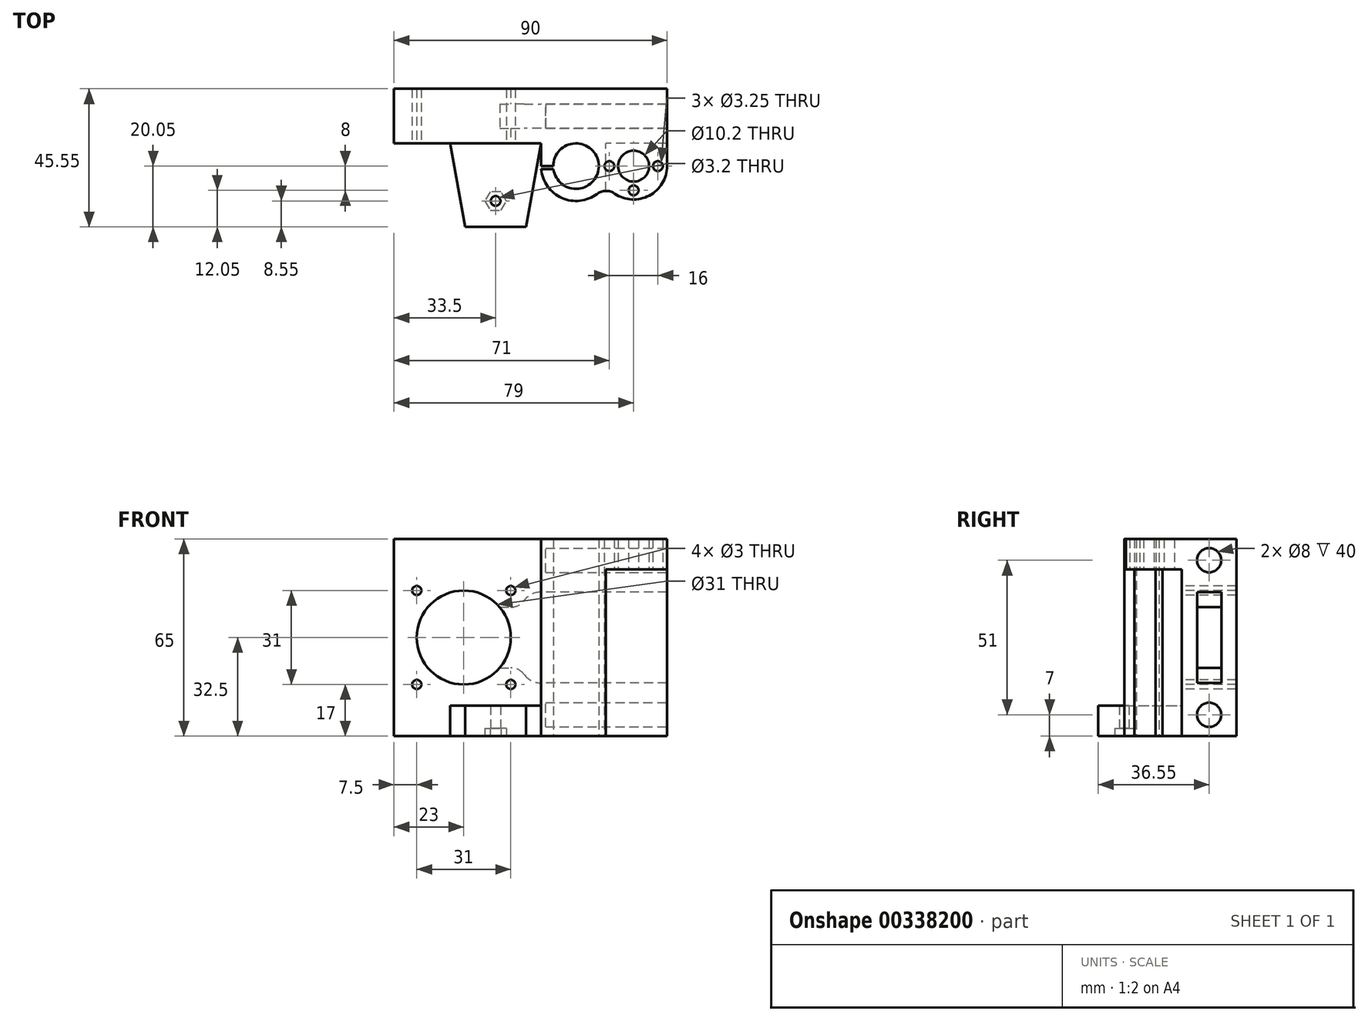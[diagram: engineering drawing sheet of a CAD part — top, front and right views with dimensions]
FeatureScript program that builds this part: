
annotation { "Feature Type Name" : "Feature", "Feature Type Description" : "" }
export const myFeature = defineFeature(function(context is Context, id is Id, definition is map)
    precondition{}
    {
        {
            var Q0;
            Q0=qCreatedBy(makeId("Top.planeOp"),FACE);
            var sketch = newSketch(context, id + "F0", { "sketchPlane" : qUnion([Q0])});
            skLineSegment(sketch, "E0.top", {"start": v(0, 18) * mm, "end": v(-90, 18) * mm});
            skLineSegment(sketch, "E0.left", {"start": v(0, 0) * mm, "end": v(0, 18) * mm});
            skLineSegment(sketch, "E0.right", {"start": v(-90, 0) * mm, "end": v(-90, 18) * mm});
            skArc(sketch, "E1", {"start": v(-17.24, -16.56) * mm, "mid": v(-5.88, -17.24) * mm, "end": v(0, -7.5) * mm});
            skLineSegment(sketch, "E2.left", {"start": v(-41.5, -7.5) * mm, "end": v(-41.5, 0) * mm});
            skLineSegment(sketch, "E2.right", {"start": v(0, -7.5) * mm, "end": v(0, 0) * mm});
            skLineSegment(sketch, "E3", {"start": v(-30, -7.5) * mm, "end": v(-11, -7.5) * mm, "construction": true});
            skCircle(sketch, "E4", {"center": v(-11, -7.5) * mm, "radius": 5.1 * mm});
            skCircle(sketch, "E5", {"center": v(-19, -7.5) * mm, "radius": 1.63 * mm});
            skCircle(sketch, "E6.1.0", {"center": v(-11, -15.5) * mm, "radius": 1.63 * mm});
            skCircle(sketch, "E6.2.0", {"center": v(-3, -7.5) * mm, "radius": 1.63 * mm});
            skArc(sketch, "E7", {"start": v(-37.43, -8.5) * mm, "mid": v(-22.52, -7) * mm, "end": v(-37.5, -7.5) * mm});
            skArc(sketch, "E8.trimOffspring", {"start": v(-41.46, -8.5) * mm, "mid": v(-34.68, -18) * mm, "end": v(-23.08, -16.69) * mm});
            skPoint(sketch, "E9.visualSharp", {"position": v(-20.2, -13.52) * mm});
            skArc(sketch, "E9.filletArc", {"start": v(-17.24, -16.56) * mm, "mid": v(-20.18, -15.68) * mm, "end": v(-23.08, -16.69) * mm});
            skLineSegment(sketch, "E10.trimOffspring", {"start": v(-41.5, 0) * mm, "end": v(-90, 0) * mm});
            skLineSegment(sketch, "E11.bottom", {"start": v(-37.5, -7.5) * mm, "end": v(-41.5, -7.5) * mm});
            skLineSegment(sketch, "E11.top", {"start": v(-37.43, -8.5) * mm, "end": v(-41.46, -8.5) * mm});
            skSolve(sketch);
        }
        {
            var Q0;
            Q0=makeQuery(id+"F0.imprint","IMPRINT",FACE,{"disambiguationData":[TD([[makeQuery(id+"F0.imprint","IMPRINT",EDGE,{"derivedFrom":sQuery(id+"F0.wireOp",EDGE,"E0.top")}),1.0]])]});
            extrude(context, id + "F1", {"entities" : qUnion([Q0]), "depth" : 65 * mm});
        }
        {
            var Q0;
            Q0=makeQuery(id+"F1.opExtrude","SWEPT_FACE",FACE,{"disambiguationData":[OSD([sQuery(id+"F0.wireOp",EDGE,"E10.trimOffspring")])]});
            var sketch = newSketch(context, id + "F2", { "sketchPlane" : qUnion([Q0])});
            skLineSegment(sketch, "E12.bottom", {"start": v(0, 0) * mm, "end": v(-20.18, 0) * mm});
            skLineSegment(sketch, "E12.top", {"start": v(0, 55) * mm, "end": v(-20.18, 55) * mm});
            skLineSegment(sketch, "E12.left", {"start": v(0, 0) * mm, "end": v(0, 55) * mm});
            skLineSegment(sketch, "E12.right", {"start": v(-20.18, 0) * mm, "end": v(-20.18, 55) * mm});
            skSolve(sketch);
        }
        {
            var Q0;
            Q0 = qSketchRegion(id + "F2", true);
            extrude(context, id + "F3", {"entities" : qUnion([Q0]), "operationType" : NewBodyOperationType.REMOVE, "endBound" : BoundingType.THROUGH_ALL, "depth" : 25 * mm});
        }
        {
            var Q0;
            Q0=makeQuery(id+"F1.opExtrude","SWEPT_FACE",FACE,{"disambiguationData":[OSD([sQuery(id+"F0.wireOp",EDGE,"E10.trimOffspring")])]});
            var sketch = newSketch(context, id + "F4", { "sketchPlane" : qUnion([Q0])});
            skCircle(sketch, "E13", {"center": v(-67, 32.5) * mm, "radius": 15.5 * mm});
            skCircle(sketch, "E14", {"center": v(-82.5, 17) * mm, "radius": 1.5 * mm});
            skLineSegment(sketch, "E15", {"start": v(-90, 17) * mm, "end": v(-67, 17) * mm, "construction": true});
            skCircle(sketch, "E16.1.0", {"center": v(-51.5, 17) * mm, "radius": 1.5 * mm});
            skCircle(sketch, "E16.2.0", {"center": v(-51.5, 48) * mm, "radius": 1.5 * mm});
            skCircle(sketch, "E16.3.0", {"center": v(-82.5, 48) * mm, "radius": 1.5 * mm});
            skSolve(sketch);
        }
        {
            var Q0;
            Q0 = qSketchRegion(id + "F4", true);
            extrude(context, id + "F5", {"entities" : qUnion([Q0]), "operationType" : NewBodyOperationType.REMOVE, "endBound" : BoundingType.THROUGH_ALL, "oppositeDirection" : true, "depth" : 25 * mm});
        }
        {
            var Q0;
            Q0=makeQuery(id+"F1.opExtrude","SWEPT_FACE",FACE,{"disambiguationData":[OSD([sQuery(id+"F0.wireOp",EDGE,"E0.left"),sQuery(id+"F0.wireOp",EDGE,"E2.right")])]});
            var sketch = newSketch(context, id + "F6", { "sketchPlane" : qUnion([Q0])});
            skLineSegment(sketch, "E17", {"start": v(9, 0) * mm, "end": v(9, 65) * mm, "construction": true});
            skLineSegment(sketch, "E18", {"start": v(18, 32.5) * mm, "end": v(0, 32.5) * mm, "construction": true});
            skPoint(sketch, "E18.endSnap0", {"position": v(9, 32.5) * mm});
            skCircle(sketch, "E19", {"center": v(9, 58) * mm, "radius": 4 * mm});
            skCircle(sketch, "E20.MirrorC", {"center": v(9, 7) * mm, "radius": 4 * mm});
            skSolve(sketch);
        }
        {
            var Q0;
            Q0 = qSketchRegion(id + "F6", true);
            extrude(context, id + "F7", {"entities" : qUnion([Q0]), "operationType" : NewBodyOperationType.REMOVE, "oppositeDirection" : true, "depth" : 40 * mm});
        }
        {
            var Q0;
            Q0=makeQuery(id+"F1.opExtrude","CAP_EDGE",EDGE,{"disambiguationData":[OSD([sQuery(id+"F0.wireOp",EDGE,"E0.right")])],"isStart":false});
            cPoint(context, id + "F8", {"entities" : qUnion([Q0]), "parameter" : 0.5});
        }
        {
            var Q0;
            Q0=makeQuery(id+"F1.opExtrude","CAP_EDGE",EDGE,{"disambiguationData":[OSD([sQuery(id+"F0.wireOp",EDGE,"E0.left"),sQuery(id+"F0.wireOp",EDGE,"E2.right")])],"isStart":true});
            cPoint(context, id + "F9", {"entities" : qUnion([Q0]), "parameter" : 0.5});
        }
        {
            var Q0;
            Q0=makeQuery(id+"F1.opExtrude","CAP_EDGE",EDGE,{"disambiguationData":[OSD([sQuery(id+"F0.wireOp",EDGE,"E0.right")])],"isStart":true});
            cPoint(context, id + "F10", {"entities" : qUnion([Q0]), "parameter" : 0.5});
        }
        {
            var Q0;
            Q0 = qCreatedBy(id + "F8" ,VERTEX);
            var Q1;
            Q1 = qCreatedBy(id + "F9" ,VERTEX);
            var Q2;
            Q2 = qCreatedBy(id + "F10" ,VERTEX);
            cPlane(context, id + "F11", {"entities" : qUnion([Q0, Q1, Q2]), "cplaneType" : CPlaneType.THREE_POINT, "offset" : 25 * mm, "width" : 150 * mm, "height" : 150 * mm});
        }
        {
            var Q0;
            Q0=qCreatedBy(id+"F11.planeOp",FACE);
            var sketch = newSketch(context, id + "F12", { "sketchPlane" : qUnion([Q0])});
            skLineSegment(sketch, "E21.bottom", {"start": v(0, 32.5) * mm, "end": v(-67, 32.5) * mm});
            skLineSegment(sketch, "E21.top", {"start": v(0, 47.5) * mm, "end": v(-41.46, 47.5) * mm});
            skLineSegment(sketch, "E21.left", {"start": v(0, 32.5) * mm, "end": v(0, 47.5) * mm});
            skLineSegment(sketch, "E22.trimOffspring", {"start": v(-90, 32.5) * mm, "end": v(0, 32.5) * mm, "construction": true});
            skLineSegment(sketch, "E23", {"start": v(-67, 32.5) * mm, "end": v(-67, 42.5) * mm});
            skLineSegment(sketch, "E24", {"start": v(-67, 42.5) * mm, "end": v(-51.5, 42.5) * mm});
            skArc(sketch, "E25", {"start": v(-51.5, 42.5) * mm, "mid": v(-49.05, 43.08) * mm, "end": v(-47.11, 44.68) * mm});
            skArc(sketch, "E26", {"start": v(-41.46, 47.5) * mm, "mid": v(-44.61, 46.76) * mm, "end": v(-47.11, 44.68) * mm});
            skLineSegment(sketch, "E27.MirrorCS", {"start": v(-67, 32.5) * mm, "end": v(-67, 22.5) * mm});
            skLineSegment(sketch, "E28.MirrorCS", {"start": v(-67, 22.5) * mm, "end": v(-51.5, 22.5) * mm});
            skArc(sketch, "E29.MirrorCS", {"start": v(-51.5, 22.5) * mm, "mid": v(-49.05, 21.92) * mm, "end": v(-47.11, 20.32) * mm});
            skArc(sketch, "E30.MirrorCS", {"start": v(-41.46, 17.5) * mm, "mid": v(-44.61, 18.24) * mm, "end": v(-47.11, 20.32) * mm});
            skLineSegment(sketch, "E31.MirrorCS", {"start": v(0, 17.5) * mm, "end": v(-41.46, 17.5) * mm});
            skLineSegment(sketch, "E32.MirrorCS", {"start": v(0, 32.5) * mm, "end": v(0, 17.5) * mm});
            skSolve(sketch);
        }
        {
            var Q0;
            Q0=makeQuery(id+"F12.imprint","IMPRINT",FACE,{"disambiguationData":[TD([[makeQuery(id+"F12.imprint","IMPRINT",EDGE,{"derivedFrom":sQuery(id+"F12.wireOp",EDGE,"E21.bottom")}),-1.0]])]});
            var Q1;
            Q1=makeQuery(id+"F12.imprint","IMPRINT",FACE,{"disambiguationData":[TD([[makeQuery(id+"F12.imprint","IMPRINT",EDGE,{"derivedFrom":sQuery(id+"F12.wireOp",EDGE,"E21.bottom")}),1.0]])]});
            extrude(context, id + "F13", {"entities" : qUnion([Q0, Q1]), "operationType" : NewBodyOperationType.REMOVE, "endBound" : BoundingType.SYMMETRIC, "oppositeDirection" : true, "depth" : 8 * mm});
        }
        {
            var Q0;
            Q0=makeQuery(id+"F1.opExtrude","CAP_FACE",FACE,{"disambiguationData":[OSD([sQuery(id+"F0.wireOp",EDGE,"E0.top"),sQuery(id+"F0.wireOp",EDGE,"E0.left"),sQuery(id+"F0.wireOp",EDGE,"E0.right"),sQuery(id+"F0.wireOp",EDGE,"E1"),sQuery(id+"F0.wireOp",EDGE,"E2.left"),sQuery(id+"F0.wireOp",EDGE,"E2.right"),sQuery(id+"F0.wireOp",EDGE,"E4"),sQuery(id+"F0.wireOp",EDGE,"E5"),sQuery(id+"F0.wireOp",EDGE,"E6.1.0"),sQuery(id+"F0.wireOp",EDGE,"E6.2.0"),sQuery(id+"F0.wireOp",EDGE,"E7"),sQuery(id+"F0.wireOp",EDGE,"E8.trimOffspring"),sQuery(id+"F0.wireOp",EDGE,"E9.filletArc"),sQuery(id+"F0.wireOp",EDGE,"E10.trimOffspring"),sQuery(id+"F0.wireOp",EDGE,"E11.bottom"),sQuery(id+"F0.wireOp",EDGE,"E11.top")])],"isStart":true});
            var sketch = newSketch(context, id + "F14", { "sketchPlane" : qUnion([Q0])});
            skLineSegment(sketch, "E33.bottom", {"start": v(-46.5, 0) * mm, "end": v(-66.5, 0) * mm});
            skLineSegment(sketch, "E33.top", {"start": v(-46.5, 27.55) * mm, "end": v(-66.5, 27.55) * mm});
            skLineSegment(sketch, "E33.left", {"start": v(-46.5, 0) * mm, "end": v(-46.5, 27.55) * mm});
            skLineSegment(sketch, "E33.right", {"start": v(-66.5, 0) * mm, "end": v(-66.5, 27.55) * mm});
            skLineSegment(sketch, "E34", {"start": v(-56.5, 19) * mm, "end": v(-30, 19) * mm, "construction": true});
            skCircle(sketch, "E35.cCircle", {"center": v(-56.5, 19) * mm, "radius": 3.55 * mm, "construction": true});
            skLineSegment(sketch, "E35.0", {"start": v(-54.72, 15.93) * mm, "end": v(-58.27, 15.93) * mm});
            skLineSegment(sketch, "E35.1", {"start": v(-58.27, 15.93) * mm, "end": v(-60.05, 19) * mm});
            skLineSegment(sketch, "E35.2", {"start": v(-60.05, 19) * mm, "end": v(-58.28, 22.07) * mm});
            skLineSegment(sketch, "E35.3", {"start": v(-58.27, 22.07) * mm, "end": v(-54.72, 22.07) * mm});
            skLineSegment(sketch, "E35.4", {"start": v(-54.72, 22.07) * mm, "end": v(-52.95, 19) * mm});
            skLineSegment(sketch, "E35.5", {"start": v(-52.95, 19) * mm, "end": v(-54.72, 15.93) * mm});
            skLineSegment(sketch, "E36", {"start": v(-56.5, 19) * mm, "end": v(-56.5, 0) * mm, "construction": true});
            skLineSegment(sketch, "E37", {"start": v(-46.5, 27.55) * mm, "end": v(-41.5, 0) * mm});
            skLineSegment(sketch, "E38.MirrorCS", {"start": v(-66.5, 27.55) * mm, "end": v(-71.5, 0) * mm});
            skLineSegment(sketch, "E39", {"start": v(-71.5, 0) * mm, "end": v(-41.5, 0) * mm});
            skSolve(sketch);
        }
        {
            var Q0;
            Q0=makeQuery(id+"F14.imprint","IMPRINT",FACE,{"disambiguationData":[TD([[makeQuery(id+"F14.imprint","IMPRINT",EDGE,{"derivedFrom":sQuery(id+"F14.wireOp",EDGE,"E33.top")}),1.0]])]});
            var Q1;
            {var subQ0=sQuery(id+"F14.wireOp",EDGE,"E33.right");Q1=makeQuery(id+"F14.imprint","IMPRINT",FACE,{"disambiguationData":[TD([[makeQuery(id+"F14.imprint","IMPRINT",EDGE,{"derivedFrom":subQ0}),1.0]])]});}
            var Q2;
            {var subQ0=sQuery(id+"F14.wireOp",EDGE,"E33.left");Q2=makeQuery(id+"F14.imprint","IMPRINT",FACE,{"disambiguationData":[TD([[makeQuery(id+"F14.imprint","IMPRINT",EDGE,{"derivedFrom":subQ0}),-1.0]])]});}
            var Q3;
            Q3=makeQuery(id+"F14.imprint","IMPRINT",FACE,{"disambiguationData":[TD([[makeQuery(id+"F14.imprint","IMPRINT",EDGE,{"derivedFrom":sQuery(id+"F14.wireOp",EDGE,"E35.0")}),-1.0]])]});
            extrude(context, id + "F15", {"entities" : qUnion([Q0, Q1, Q2, Q3]), "operationType" : NewBodyOperationType.ADD, "oppositeDirection" : true, "depth" : 10 * mm});
        }
        {
            var Q0;
            Q0=makeQuery(id+"F14.imprint","IMPRINT",FACE,{"disambiguationData":[TD([[makeQuery(id+"F14.imprint","IMPRINT",EDGE,{"derivedFrom":sQuery(id+"F14.wireOp",EDGE,"E35.0")}),-1.0]])]});
            extrude(context, id + "F16", {"entities" : qUnion([Q0]), "operationType" : NewBodyOperationType.REMOVE, "oppositeDirection" : true, "depth" : 2.5 * mm});
        }
        {
            var Q0;
            Q0=makeQuery(id+"F16.boolean.opBoolean","COPY",FACE,{"derivedFrom":makeQuery(id+"F16.opExtrude","CAP_FACE",FACE,{"disambiguationData":[OSD([sQuery(id+"F14.wireOp",EDGE,"E35.0"),sQuery(id+"F14.wireOp",EDGE,"E35.1"),sQuery(id+"F14.wireOp",EDGE,"E35.2"),sQuery(id+"F14.wireOp",EDGE,"E35.3"),sQuery(id+"F14.wireOp",EDGE,"E35.4"),sQuery(id+"F14.wireOp",EDGE,"E35.5")])],"isStart":false})});
            var sketch = newSketch(context, id + "F17", { "sketchPlane" : qUnion([Q0])});
            skCircle(sketch, "E40", {"center": v(-56.5, 19) * mm, "radius": 1.6 * mm});
            skPoint(sketch, "E40.centerSnap0", {"position": v(-56.5, 15.93) * mm});
            skLineSegment(sketch, "E41", {"start": v(-56.5, 15.93) * mm, "end": v(-56.5, 22.07) * mm, "construction": true});
            skLineSegment(sketch, "E42", {"start": v(-60.05, 19) * mm, "end": v(-52.95, 19) * mm, "construction": true});
            skSolve(sketch);
        }
        {
            var Q0;
            Q0=makeQuery(id+"F17.imprint","IMPRINT",FACE,{"disambiguationData":[TD([[makeQuery(id+"F17.imprint","IMPRINT",EDGE,{"derivedFrom":sQuery(id+"F17.wireOp",EDGE,"E40")}),1.0]])]});
            extrude(context, id + "F18", {"entities" : qUnion([Q0]), "operationType" : NewBodyOperationType.REMOVE, "endBound" : BoundingType.THROUGH_ALL, "oppositeDirection" : true, "depth" : 25 * mm});
        }
    });
